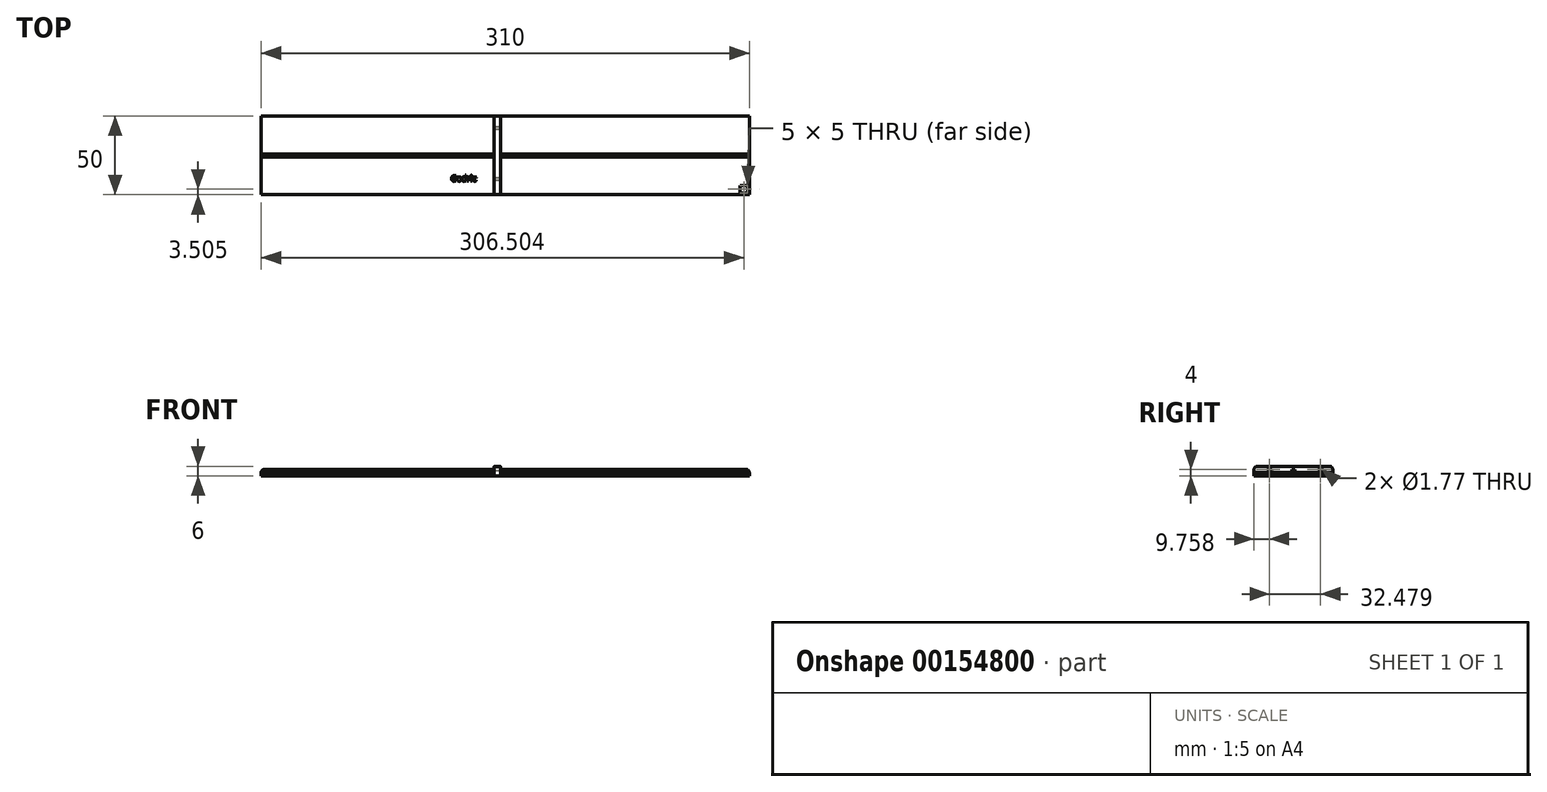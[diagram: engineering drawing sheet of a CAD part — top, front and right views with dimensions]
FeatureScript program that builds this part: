
annotation { "Feature Type Name" : "Feature", "Feature Type Description" : "" }
export const myFeature = defineFeature(function(context is Context, id is Id, definition is map)
    precondition{}
    {
        {
            var Q0;
            Q0=qCreatedBy(makeId("Top.planeOp"),FACE);
            var sketch = newSketch(context, id + "F0", { "sketchPlane" : qUnion([Q0])});
            skLineSegment(sketch, "E0.bottom", {"start": v(-235.9, 31.15) * mm, "end": v(74.1, 31.15) * mm});
            skLineSegment(sketch, "E0.left", {"start": v(-235.9, 31.15) * mm, "end": v(-235.9, -18.85) * mm});
            skLineSegment(sketch, "E0.right", {"start": v(74.1, 31.15) * mm, "end": v(74.1, -18.85) * mm});
            skLineSegment(sketch, "E1.0", {"start": v(68.1, -17.85) * mm, "end": v(73.1, -17.85) * mm});
            skLineSegment(sketch, "E2.trimOffspring", {"start": v(73.1, -12.85) * mm, "end": v(73.1, -17.85) * mm});
            skLineSegment(sketch, "E3", {"start": v(74.1, -18.85) * mm, "end": v(-235.9, -18.85) * mm});
            skLineSegment(sketch, "E4.0", {"start": v(-234.9, 7.15) * mm, "end": v(-87.9, 7.15) * mm});
            skLineSegment(sketch, "E5.0", {"start": v(-234.9, 5.15) * mm, "end": v(-87.9, 5.15) * mm});
            skLineSegment(sketch, "E6.0", {"start": v(-83.9, 31.15) * mm, "end": v(-83.9, -18.85) * mm});
            skLineSegment(sketch, "E7.0", {"start": v(-87.9, 31.15) * mm, "end": v(-87.9, -18.85) * mm});
            skLineSegment(sketch, "E8.trimOffspring", {"start": v(-83.9, 5.15) * mm, "end": v(64.1, 5.15) * mm});
            skLineSegment(sketch, "E9.trimOffspring", {"start": v(-83.9, 7.15) * mm, "end": v(64.1, 7.15) * mm});
            skLineSegment(sketch, "E10", {"start": v(-234.9, 7.15) * mm, "end": v(-235.9, 7.15) * mm});
            skLineSegment(sketch, "E11", {"start": v(-234.9, 5.15) * mm, "end": v(-235.9, 5.15) * mm});
            skLineSegment(sketch, "E12", {"start": v(64.1, 7.15) * mm, "end": v(74.1, 7.15) * mm});
            skLineSegment(sketch, "E13", {"start": v(64.1, 5.15) * mm, "end": v(74.1, 5.15) * mm});
            skLineSegment(sketch, "E14", {"start": v(68.1, -17.85) * mm, "end": v(68.1, -12.85) * mm});
            skLineSegment(sketch, "E15", {"start": v(68.1, -12.85) * mm, "end": v(73.1, -12.85) * mm});
            skLineSegment(sketch, "E16", {"start": v(-235.9, 5.15) * mm, "end": v(-235.9, 7.15) * mm});
            skLineSegment(sketch, "E17", {"start": v(-235.9, 7.15) * mm, "end": v(-235.9, 31.15) * mm});
            skText(sketch, "E18", { "text": "Godric", "fontName": "OpenSans-Bold.ttf"});
            const initialGuessF0  = {"E18": [-0.11532, -0.01026, 1, 0, 0.0036]};
            skSetInitialGuess(sketch, initialGuessF0);
            skSolve(sketch);
        }
        {
            var Q0;
            {var subQ1=sQuery(id+"F0.wireOp",EDGE,"E4.0");Q0=makeQuery(id+"F0.imprint","IMPRINT",FACE,{"disambiguationData":[TD([[makeQuery(id+"F0.imprint","IMPRINT",EDGE,{"derivedFrom":subQ1}),1.0]])]});}
            var Q1;
            {var subQ4=sQuery(id+"F0.wireOp",EDGE,"E9.trimOffspring");Q1=makeQuery(id+"F0.imprint","IMPRINT",FACE,{"disambiguationData":[TD([[makeQuery(id+"F0.imprint","IMPRINT",EDGE,{"derivedFrom":subQ4}),1.0]])]});}
            var Q2;
            {var subQ0=sQuery(id+"F0.wireOp",EDGE,"E5.0");Q2=makeQuery(id+"F0.imprint","IMPRINT",FACE,{"disambiguationData":[TD([[makeQuery(id+"F0.imprint","IMPRINT",EDGE,{"derivedFrom":subQ0}),-1.0]])]});}
            var Q3;
            Q3=makeQuery(id+"F0.imprint","IMPRINT",FACE,{"disambiguationData":[TD([[makeQuery(id+"F0.imprint","IMPRINT",EDGE,{"derivedFrom":sQuery(id+"F0.wireOp",EDGE,"E1.0")}),-1.0]])]});
            extrude(context, id + "F1", {"entities" : qUnion([Q0, Q1, Q2, Q3]), "depth" : 2 * mm});
        }
        {
            var Q0;
            {var subQ1=sQuery(id+"F0.wireOp",EDGE,"E4.0");Q0=makeQuery(id+"F0.imprint","IMPRINT",FACE,{"disambiguationData":[TD([[makeQuery(id+"F0.imprint","IMPRINT",EDGE,{"derivedFrom":subQ1}),-1.0]])]});}
            var Q1;
            {var subQ1=sQuery(id+"F0.wireOp",EDGE,"E8.trimOffspring");Q1=makeQuery(id+"F0.imprint","IMPRINT",FACE,{"disambiguationData":[TD([[makeQuery(id+"F0.imprint","IMPRINT",EDGE,{"derivedFrom":subQ1}),1.0]])]});}
            extrude(context, id + "F2", {"entities" : qUnion([Q0, Q1]), "depth" : 4 * mm});
        }
        {
            var Q0;
            {var subQ0=sQuery(id+"F0.wireOp",EDGE,"E6.0");var subQ5=sQuery(id+"F0.wireOp",EDGE,"E0.bottom");var subQ6=makeQuery(id+"F0.imprint","INTERSECT",VERTEX,{"derivedFrom":[subQ5,subQ0]});Q0=makeQuery(id+"F0.imprint","IMPRINT",FACE,{"disambiguationData":[TD([[makeQuery(id+"F0.imprint","IMPRINT",EDGE,{"disambiguationData":[TD([[subQ6,1.0]])],"derivedFrom":subQ5}),-1.0]])]});}
            extrude(context, id + "F3", {"entities" : qUnion([Q0]), "depth" : 6 * mm});
        }
        {
            var Q0;
            Q0=makeQuery(id+"F3.opExtrude","SWEPT_FACE",FACE,{"disambiguationData":[OSD([sQuery(id+"F0.wireOp",EDGE,"E7.0")])]});
            var sketch = newSketch(context, id + "F4", { "sketchPlane" : qUnion([Q0])});
            skCircle(sketch, "E19", {"center": v(-23.39, 4) * mm, "radius": 0.89 * mm});
            skCircle(sketch, "E20", {"center": v(9.1, 4) * mm, "radius": 0.89 * mm});
            skSolve(sketch);
        }
        {
            var Q0;
            Q0=makeQuery(id+"F4.imprint","IMPRINT",FACE,{"disambiguationData":[TD([[makeQuery(id+"F4.imprint","IMPRINT",EDGE,{"derivedFrom":sQuery(id+"F4.wireOp",EDGE,"E19")}),1.0]])]});
            var Q1;
            Q1=makeQuery(id+"F4.imprint","IMPRINT",FACE,{"disambiguationData":[TD([[makeQuery(id+"F4.imprint","IMPRINT",EDGE,{"derivedFrom":sQuery(id+"F4.wireOp",EDGE,"E20")}),1.0]])]});
            extrude(context, id + "F5", {"entities" : qUnion([Q0, Q1]), "operationType" : NewBodyOperationType.REMOVE, "oppositeDirection" : true, "depth" : 30.27 * mm});
        }
        {
            var Q0;
            Q0=makeQuery(id+"F3.opExtrude","CAP_EDGE",EDGE,{"disambiguationData":[OSD([sQuery(id+"F0.wireOp",EDGE,"E0.bottom")])],"isStart":false});
            var Q1;
            Q1=makeQuery(id+"F3.opExtrude","CAP_EDGE",EDGE,{"disambiguationData":[OSD([sQuery(id+"F0.wireOp",EDGE,"E3")])],"isStart":false});
            var Q2;
            Q2=makeQuery(id+"F2.opExtrude","CAP_EDGE",EDGE,{"disambiguationData":[OSD([sQuery(id+"F0.wireOp",EDGE,"E0.left")])],"isStart":false});
            var Q3;
            Q3=makeQuery(id+"F2.opExtrude","CAP_EDGE",EDGE,{"disambiguationData":[OSD([sQuery(id+"F0.wireOp",EDGE,"E0.right")])],"isStart":false});
            fillet(context, id + "F6", {"entities" : qUnion([Q0, Q1, Q2, Q3]), "radius" : 2 * mm, "tangentPropagation" : true, "allowEdgeOverflow" : false});
        }
        {
            var Q0;
            Q0=makeQuery(id+"F0.imprint","IMPRINT",FACE,{"disambiguationData":[TD([[makeQuery(id+"F0.imprint","IMPRINT",EDGE,{"derivedFrom":sQuery(id+"F0.wireOp",EDGE,"E18.sketch_text.stroke-0")}),-1.0]])]});
            var Q1;
            Q1=makeQuery(id+"F0.imprint","IMPRINT",FACE,{"disambiguationData":[TD([[makeQuery(id+"F0.imprint","IMPRINT",EDGE,{"derivedFrom":sQuery(id+"F0.wireOp",EDGE,"E18.sketch_text.stroke-19")}),-1.0]])]});
            var Q2;
            Q2=makeQuery(id+"F0.imprint","IMPRINT",FACE,{"disambiguationData":[TD([[makeQuery(id+"F0.imprint","IMPRINT",EDGE,{"derivedFrom":sQuery(id+"F0.wireOp",EDGE,"E18.sketch_text.stroke-19")}),1.0]])]});
            var Q3;
            Q3=makeQuery(id+"F0.imprint","IMPRINT",FACE,{"disambiguationData":[TD([[makeQuery(id+"F0.imprint","IMPRINT",EDGE,{"derivedFrom":sQuery(id+"F0.wireOp",EDGE,"E18.sketch_text.stroke-37")}),-1.0]])]});
            var Q4;
            Q4=makeQuery(id+"F0.imprint","IMPRINT",FACE,{"disambiguationData":[TD([[makeQuery(id+"F0.imprint","IMPRINT",EDGE,{"derivedFrom":sQuery(id+"F0.wireOp",EDGE,"E18.sketch_text.stroke-51")}),1.0]])]});
            var Q5;
            Q5=makeQuery(id+"F0.imprint","IMPRINT",FACE,{"disambiguationData":[TD([[makeQuery(id+"F0.imprint","IMPRINT",EDGE,{"derivedFrom":sQuery(id+"F0.wireOp",EDGE,"E18.sketch_text.stroke-60")}),-1.0]])]});
            var Q6;
            Q6=makeQuery(id+"F0.imprint","IMPRINT",FACE,{"disambiguationData":[TD([[makeQuery(id+"F0.imprint","IMPRINT",EDGE,{"derivedFrom":sQuery(id+"F0.wireOp",EDGE,"E18.sketch_text.stroke-73")}),-1.0]])]});
            var Q7;
            Q7=makeQuery(id+"F0.imprint","IMPRINT",FACE,{"disambiguationData":[TD([[makeQuery(id+"F0.imprint","IMPRINT",EDGE,{"derivedFrom":sQuery(id+"F0.wireOp",EDGE,"E18.sketch_text.stroke-78")}),-1.0]])]});
            var Q8;
            Q8=makeQuery(id+"F0.imprint","IMPRINT",FACE,{"disambiguationData":[TD([[makeQuery(id+"F0.imprint","IMPRINT",EDGE,{"derivedFrom":sQuery(id+"F0.wireOp",EDGE,"E18.sketch_text.stroke-82")}),-1.0]])]});
            extrude(context, id + "F7", {"entities" : qUnion([Q0, Q1, Q2, Q3, Q4, Q5, Q6, Q7, Q8]), "operationType" : NewBodyOperationType.ADD, "depth" : 3 * mm});
        }
    });
